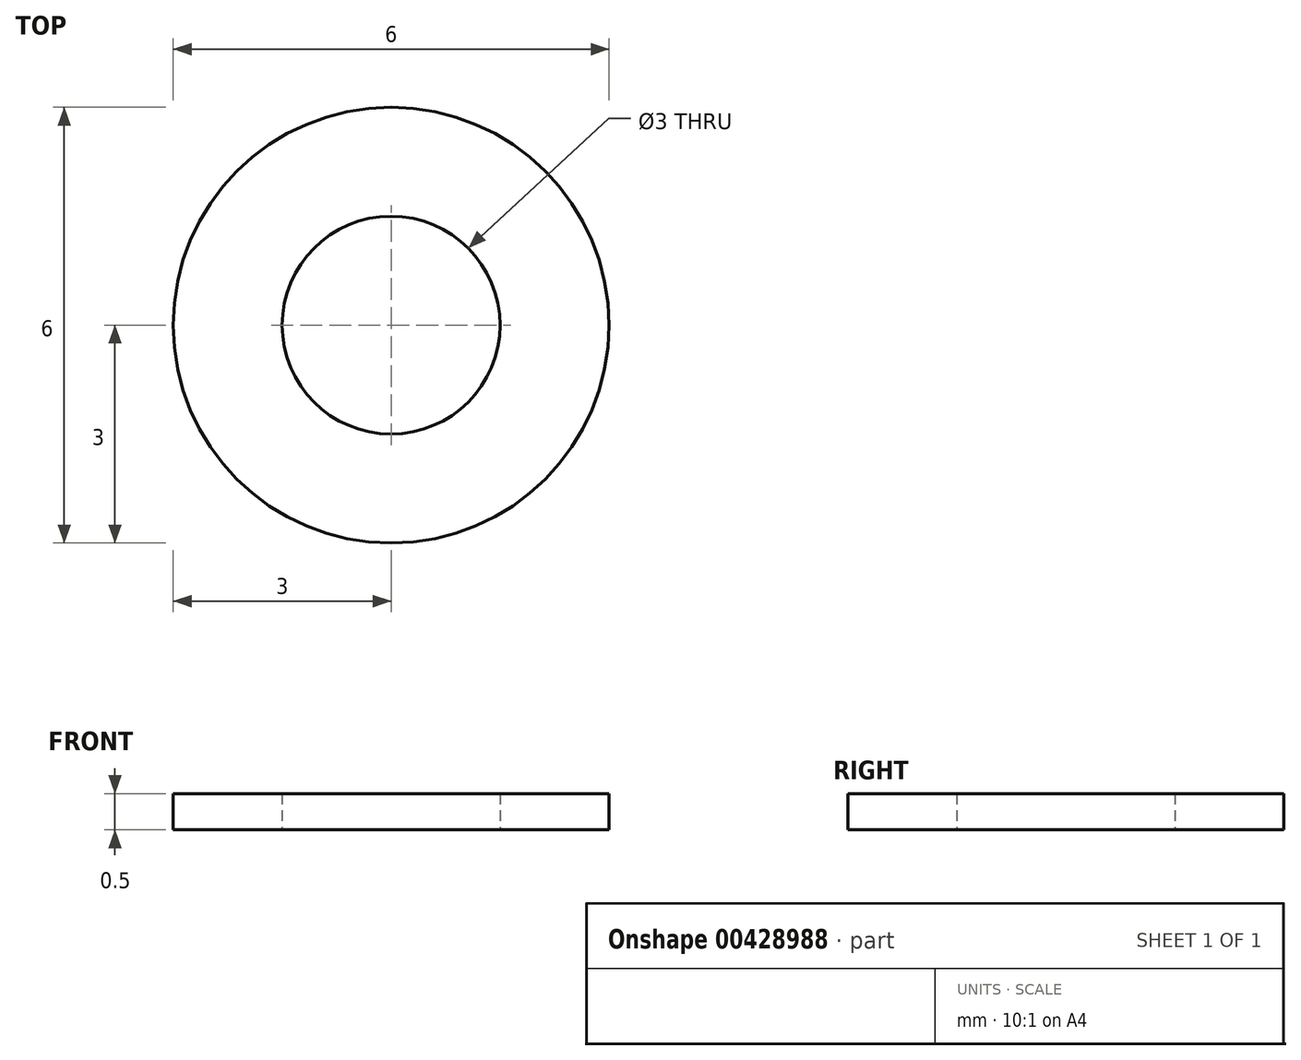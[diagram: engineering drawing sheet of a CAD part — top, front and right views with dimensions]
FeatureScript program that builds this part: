
annotation { "Feature Type Name" : "Feature", "Feature Type Description" : "" }
export const myFeature = defineFeature(function(context is Context, id is Id, definition is map)
    precondition{}
    {
        {
            var Q0;
            Q0=qCreatedBy(makeId("Top.planeOp"),FACE);
            var sketch = newSketch(context, id + "F0", { "sketchPlane" : qUnion([Q0])});
            skCircle(sketch, "E0", {"center": v(0, 0) * mm, "radius": 3 * mm});
            skCircle(sketch, "E1", {"center": v(0, 0) * mm, "radius": 1.5 * mm});
            skSolve(sketch);
        }
        {
            var Q0;
            Q0 = qSketchRegion(id + "F0", true);
            extrude(context, id + "F1", {"entities" : qUnion([Q0]), "depth" : 0.5 * mm});
        }
    });
